# Revit family: Showerhead-American_Standard-Institutional-1660.244
name_source: partatom
category: Plumbing Fixtures
revit_build: Autodesk Revit 2014 (Build: 20130308_1515(x64)
units: mm (PartAtom-declared; Revit-internal decimal feet)

## types (1)
- 1660.224
    Assembly Code = D2010710
    CW Connection = Yes
    CWFU = 2
    Cold Water Connection Diameter = 1/2"
    Cold Water Connection Radius = 1/4"
    Default Elevation = 74"
    Description = Institutional Showerhead.
    Flow Rate = 1.25gpm (5.7 Lpm)
    HW Connection = Yes
    HWFU = 3
    Height = 2 9/16"
    Length = 3 1/2"
    Manufacturer = American Standard
    Material = Brass-American Standard-002-Polished Chrome
    Model = 1660.224
    Price = Prices may vary. Please consult Manufacturer Representative for most up-to-date price list.
    Product Documentation Link = http://www.americanstandard.ca
    Revised Date = 11/23/2016
    URL = http://www.americanstandard-us.com
    Vent Connection = No
    WFU = 4
    Warranty Information = 5 year limited warranty for commercial installations.
    Waste Connection = Yes
    Width = 2 1/4"

## geometry (parser evidence)
native form markers: Sweep x3
no freeform markers — native parametric forms only
